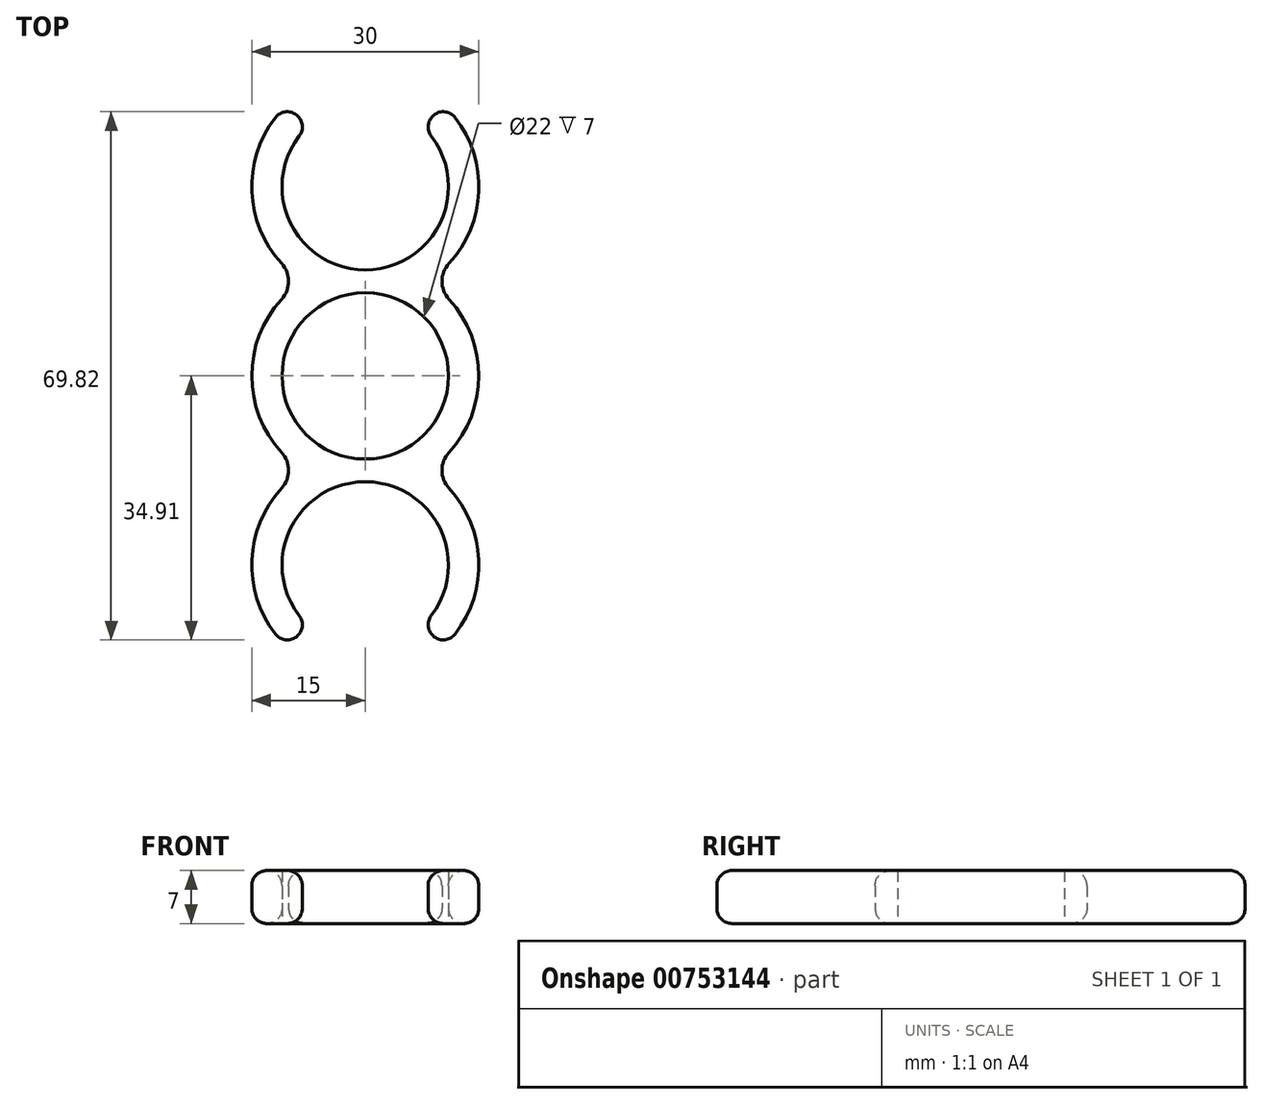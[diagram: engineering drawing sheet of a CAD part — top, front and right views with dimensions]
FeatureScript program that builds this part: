
annotation { "Feature Type Name" : "Feature", "Feature Type Description" : "" }
export const myFeature = defineFeature(function(context is Context, id is Id, definition is map)
    precondition{}
    {
        {
            var Q0;
            Q0=qCreatedBy(makeId("Top.planeOp"),FACE);
            var sketch = newSketch(context, id + "F0", { "sketchPlane" : qUnion([Q0])});
            skCircle(sketch, "E0", {"center": v(0, 0) * mm, "radius": 11 * mm});
            skArc(sketch, "E1", {"start": v(-8.73, 31.7) * mm, "mid": v(0, 14) * mm, "end": v(8.73, 31.7) * mm});
            skArc(sketch, "E2", {"start": v(8.73, -31.7) * mm, "mid": v(0, -14) * mm, "end": v(-8.73, -31.7) * mm});
            skArc(sketch, "E3", {"start": v(11.06, 14.86) * mm, "mid": v(14.99, 24.34) * mm, "end": v(11.9, 34.13) * mm});
            skArc(sketch, "E4", {"start": v(-11.06, 10.14) * mm, "mid": v(-15, 0) * mm, "end": v(-11.06, -10.14) * mm});
            skArc(sketch, "E5", {"start": v(-11.06, -14.86) * mm, "mid": v(-14.99, -24.34) * mm, "end": v(-11.9, -34.13) * mm});
            skArc(sketch, "E6.trimOffspring", {"start": v(11.06, -10.14) * mm, "mid": v(15, 0) * mm, "end": v(11.06, 10.14) * mm});
            skPoint(sketch, "E7.visualSharp", {"position": v(8.3, 12.5) * mm});
            skArc(sketch, "E7.filletArc", {"start": v(11.06, 14.86) * mm, "mid": v(10.14, 12.5) * mm, "end": v(11.06, 10.14) * mm});
            skPoint(sketch, "E8.visualSharp", {"position": v(-8.3, 12.5) * mm});
            skArc(sketch, "E8.filletArc", {"start": v(-11.06, 10.14) * mm, "mid": v(-10.14, 12.5) * mm, "end": v(-11.06, 14.86) * mm});
            skPoint(sketch, "E9.visualSharp", {"position": v(-8.3, -12.5) * mm});
            skArc(sketch, "E9.filletArc", {"start": v(-11.06, -14.86) * mm, "mid": v(-10.14, -12.5) * mm, "end": v(-11.06, -10.14) * mm});
            skPoint(sketch, "E10.visualSharp", {"position": v(8.3, -12.5) * mm});
            skArc(sketch, "E10.filletArc", {"start": v(11.06, -10.14) * mm, "mid": v(10.14, -12.5) * mm, "end": v(11.06, -14.86) * mm});
            skLineSegment(sketch, "E11", {"start": v(11.9, 34.13) * mm, "end": v(8.73, 31.7) * mm, "construction": true});
            skLineSegment(sketch, "E12", {"start": v(-8.73, 31.7) * mm, "end": v(-11.9, 34.13) * mm, "construction": true});
            skLineSegment(sketch, "E13", {"start": v(-8.73, 31.7) * mm, "end": v(8.73, 31.7) * mm, "construction": true});
            skArc(sketch, "E14.trimOffspring", {"start": v(11.9, -34.13) * mm, "mid": v(14.99, -24.34) * mm, "end": v(11.06, -14.86) * mm});
            skArc(sketch, "E15.trimOffspring", {"start": v(-11.9, 34.13) * mm, "mid": v(-14.99, 24.34) * mm, "end": v(-11.06, 14.86) * mm});
            skArc(sketch, "E16", {"start": v(-11.9, -34.13) * mm, "mid": v(-9.1, -34.5) * mm, "end": v(-8.73, -31.7) * mm});
            skLineSegment(sketch, "E17", {"start": v(0, -25) * mm, "end": v(-8.73, -31.7) * mm, "construction": true});
            skLineSegment(sketch, "E18", {"start": v(-8.73, -31.7) * mm, "end": v(-11.9, -34.13) * mm, "construction": true});
            skArc(sketch, "E19", {"start": v(8.73, -31.7) * mm, "mid": v(9.1, -34.5) * mm, "end": v(11.9, -34.13) * mm});
            skLineSegment(sketch, "E20", {"start": v(0, -25) * mm, "end": v(8.73, -31.7) * mm, "construction": true});
            skLineSegment(sketch, "E21", {"start": v(11.9, -34.13) * mm, "end": v(8.73, -31.7) * mm, "construction": true});
            skLineSegment(sketch, "E22", {"start": v(-8.73, -31.7) * mm, "end": v(8.73, -31.7) * mm, "construction": true});
            skArc(sketch, "E23", {"start": v(-8.73, 31.7) * mm, "mid": v(-9.1, 34.5) * mm, "end": v(-11.9, 34.13) * mm});
            skArc(sketch, "E24", {"start": v(11.9, 34.13) * mm, "mid": v(9.1, 34.5) * mm, "end": v(8.73, 31.7) * mm});
            skLineSegment(sketch, "E25", {"start": v(-8.73, 31.7) * mm, "end": v(0, 25) * mm, "construction": true});
            skLineSegment(sketch, "E26", {"start": v(8.73, 31.7) * mm, "end": v(0, 25) * mm, "construction": true});
            skSolve(sketch);
        }
        {
            var Q0;
            Q0 = qSketchRegion(id + "F0", true);
            extrude(context, id + "F1", {"entities" : qUnion([Q0]), "depth" : 7 * mm, "offsetDistance" : 25 * mm});
        }
        {
            var Q0;
            Q0=makeQuery(id+"F1.opExtrude","CAP_EDGE",EDGE,{"disambiguationData":[OSD([sQuery(id+"F0.wireOp",EDGE,"E3")])],"isStart":false});
            var Q1;
            Q1=makeQuery(id+"F1.opExtrude","CAP_EDGE",EDGE,{"disambiguationData":[OSD([sQuery(id+"F0.wireOp",EDGE,"E3")])],"isStart":true});
            fillet(context, id + "F2", {"entities" : qUnion([Q0, Q1]), "radius" : 2 * mm, "tangentPropagation" : true, "allowEdgeOverflow" : false});
        }
    });
